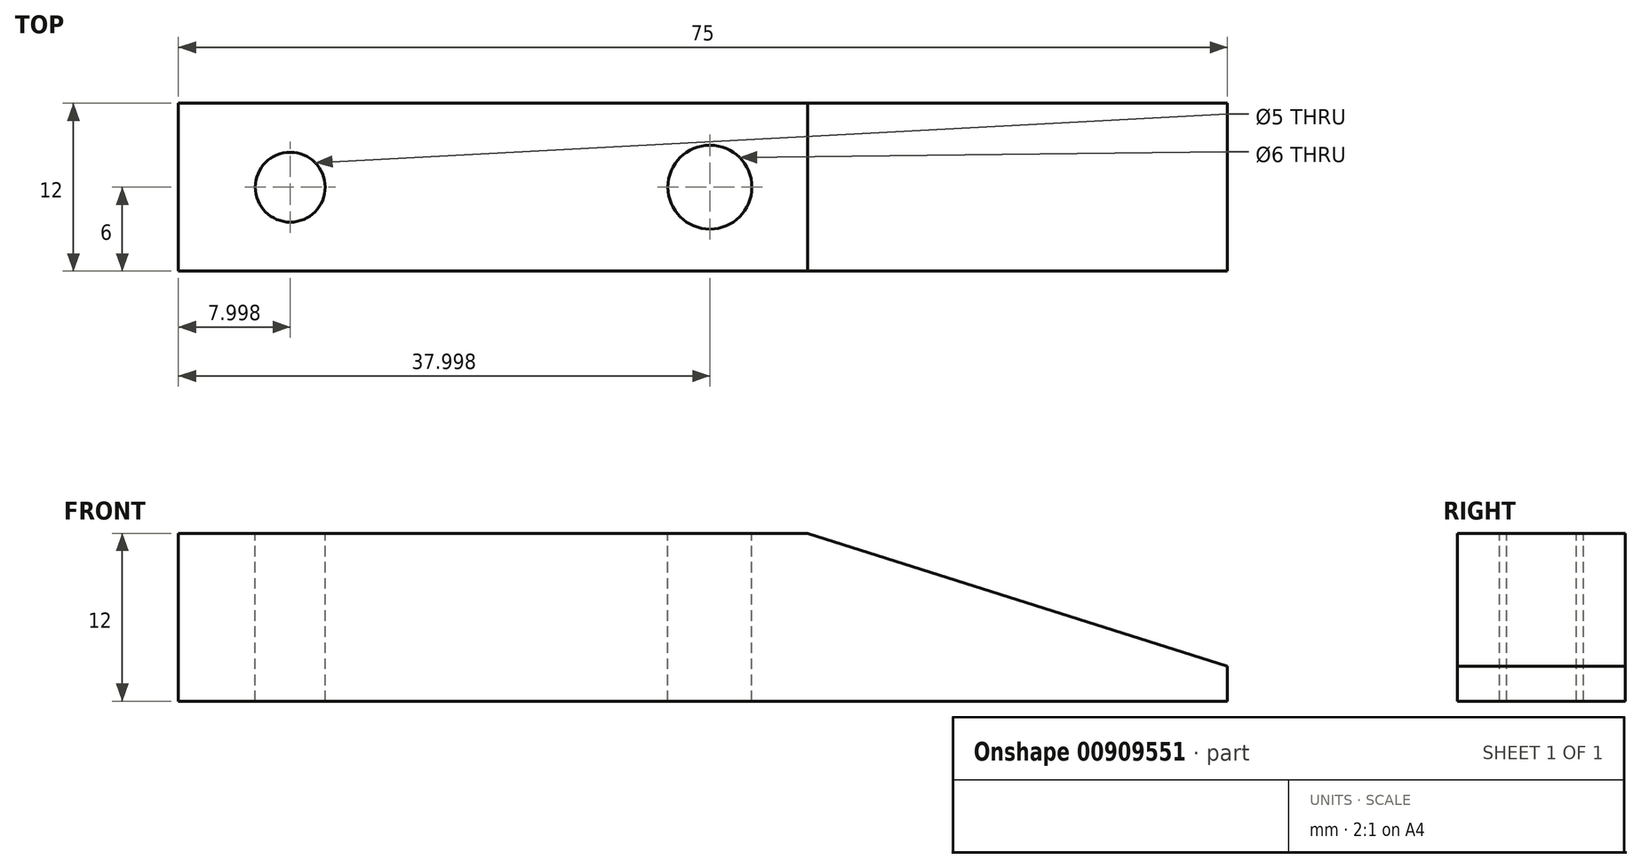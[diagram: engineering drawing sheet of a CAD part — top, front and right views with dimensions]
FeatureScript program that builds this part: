
annotation { "Feature Type Name" : "Feature", "Feature Type Description" : "" }
export const myFeature = defineFeature(function(context is Context, id is Id, definition is map)
    precondition{}
    {
        {
            var Q0;
            Q0=qCreatedBy(makeId("Front.planeOp"),FACE);
            var sketch = newSketch(context, id + "F0", { "sketchPlane" : qUnion([Q0])});
            skLineSegment(sketch, "E0", {"start": v(-40.75, 14.53) * mm, "end": v(-40.75, 2.53) * mm});
            skLineSegment(sketch, "E1", {"start": v(-40.75, 2.53) * mm, "end": v(34.25, 2.53) * mm});
            skLineSegment(sketch, "E2", {"start": v(34.25, 2.53) * mm, "end": v(34.25, 5.03) * mm});
            skLineSegment(sketch, "E3", {"start": v(34.25, 5.03) * mm, "end": v(4.25, 14.53) * mm});
            skLineSegment(sketch, "E4", {"start": v(4.25, 14.53) * mm, "end": v(-40.75, 14.53) * mm});
            skSolve(sketch);
        }
        {
            var Q0;
            Q0 = qSketchRegion(id + "F0", true);
            extrude(context, id + "F1", {"entities" : qUnion([Q0]), "depth" : 12 * mm, "offsetDistance" : 25 * mm});
        }
        {
            var Q0;
            Q0=makeQuery(id+"F1.opExtrude","SWEPT_FACE",FACE,{"disambiguationData":[OSD([sQuery(id+"F0.wireOp",EDGE,"E4")])]});
            var sketch = newSketch(context, id + "F2", { "sketchPlane" : qUnion([Q0])});
            skCircle(sketch, "E5", {"center": v(-2.75, -6) * mm, "radius": 3 * mm});
            skCircle(sketch, "E6", {"center": v(-32.75, -6) * mm, "radius": 2.5 * mm});
            skSolve(sketch);
        }
        {
            var Q0;
            Q0 = qSketchRegion(id + "F2", true);
            extrude(context, id + "F3", {"entities" : qUnion([Q0]), "operationType" : NewBodyOperationType.REMOVE, "endBound" : BoundingType.THROUGH_ALL, "oppositeDirection" : true, "depth" : 25 * mm, "offsetDistance" : 25 * mm});
        }
    });
